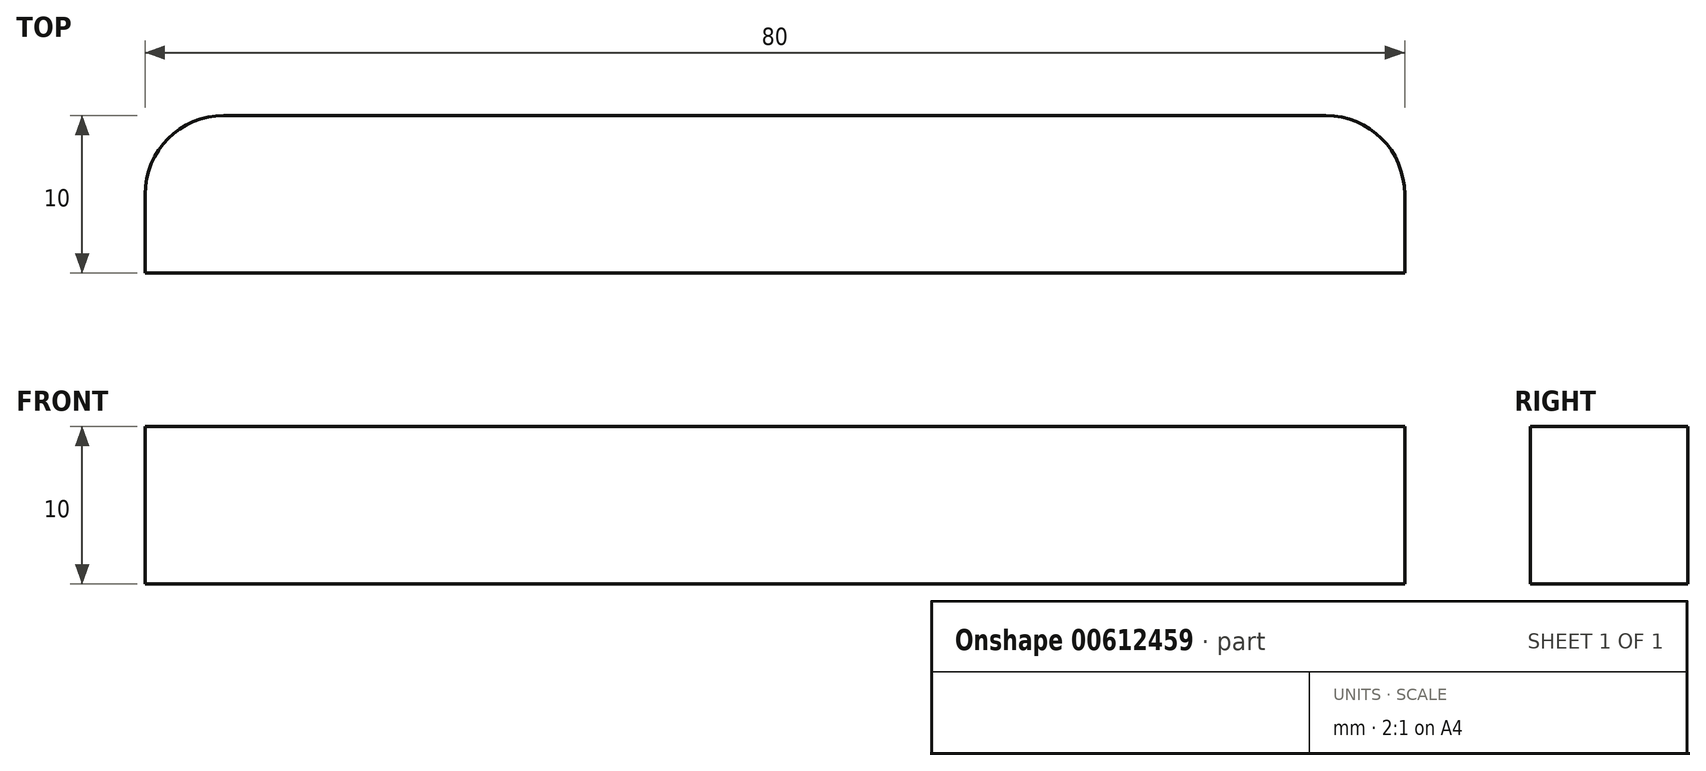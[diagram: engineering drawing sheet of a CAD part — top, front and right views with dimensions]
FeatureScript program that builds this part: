
annotation { "Feature Type Name" : "Feature", "Feature Type Description" : "" }
export const myFeature = defineFeature(function(context is Context, id is Id, definition is map)
    precondition{}
    {
        {
            var Q0;
            Q0=qCreatedBy(makeId("Top.planeOp"),FACE);
            var sketch = newSketch(context, id + "F0", { "sketchPlane" : qUnion([Q0])});
            skLineSegment(sketch, "E0.bottom", {"start": v(-40, 10) * mm, "end": v(40, 10) * mm});
            skLineSegment(sketch, "E0.top", {"start": v(-40, 0) * mm, "end": v(40, 0) * mm});
            skLineSegment(sketch, "E0.left", {"start": v(-40, 10) * mm, "end": v(-40, 0) * mm});
            skLineSegment(sketch, "E0.right", {"start": v(40, 10) * mm, "end": v(40, 0) * mm});
            skLineSegment(sketch, "E1.bottom", {"start": v(-10, 10) * mm, "end": v(10, 10) * mm});
            skLineSegment(sketch, "E1.top", {"start": v(-10, 65) * mm, "end": v(10, 65) * mm});
            skLineSegment(sketch, "E1.left", {"start": v(-10, 10) * mm, "end": v(-10, 65) * mm});
            skLineSegment(sketch, "E1.right", {"start": v(10, 10) * mm, "end": v(10, 65) * mm});
            skSolve(sketch);
        }
        {
            var Q0;
            Q0=makeQuery(id+"F0.imprint","IMPRINT",FACE,{"disambiguationData":[TD([[makeQuery(id+"F0.imprint","IMPRINT",EDGE,{"derivedFrom":sQuery(id+"F0.wireOp",EDGE,"E0.top")}),1.0]])]});
            var Q1;
            Q1=makeQuery(id+"F0.imprint","IMPRINT",FACE,{"disambiguationData":[TD([[makeQuery(id+"F0.imprint","IMPRINT",EDGE,{"derivedFrom":sQuery(id+"F0.wireOp",EDGE,"E1.bottom")}),1.0]])]});
            extrude(context, id + "F1", {"entities" : qUnion([Q0, Q1]), "depth" : 10 * mm, "offsetDistance" : 25 * mm});
        }
        {
            var Q0;
            Q0=makeQuery(id+"F1.opExtrude","SWEPT_EDGE",EDGE,{"disambiguationData":[OSD([sQuery(id+"F0.wireOp",EDGE,"E0.bottom"),sQuery(id+"F0.wireOp",EDGE,"E0.left")])]});
            var Q1;
            Q1=makeQuery(id+"F1.opExtrude","SWEPT_EDGE",EDGE,{"disambiguationData":[OSD([sQuery(id+"F0.wireOp",EDGE,"E0.bottom"),sQuery(id+"F0.wireOp",EDGE,"E0.right")])]});
            fillet(context, id + "F2", {"entities" : qUnion([Q0, Q1]), "radius" : 5 * mm, "tangentPropagation" : true, "allowEdgeOverflow" : false});
        }
    });
